# Revit family: Sanitary_Taps-And-Mixers_Sanindusa_Line-42_Wall-Concealed-Basin-Mixer
name_source: partatom
category: Plumbing Fixtures
revit_build: Autodesk Revit 2018 (Build: 20170223_1515(x64)
units: mm (PartAtom-declared; Revit-internal decimal feet)

## family parameters
Cut with Voids When Loaded = No
Host = Face
Part Type = Normal
Room Calculation Point = No
Round Connector Dimension = Use Diameter
Shared = No

## types (1)
- Sanitary_Taps-And-Mixers_Sanindusa_Line-42_Wall-Concealed-Basin-Mixer
    AssetType = Fixed
    BodyMaterial = Brass
    CartridgeType = D35 mm closed ceramic cartridge
    Color = Silver
    Constituents = Single lever concealed basin mixer.  2 x M/F 10/1x1/2 350mm stainless steel flexible supply hoses.
    Default Elevation = 1219 mm
    Description = A small diameter valve, with a free outlet, from which water is drawn.
    Element Type = FAUCET: A small diameter valve, with a free outlet, from which water is drawn.
    FaucetFunction = Mixed
    FaucetOperation = Other
    FaucetTopDescription = Single lever
    FaucetType = SprayMixing
    Features = Ceramic cartridge technology. Single lever mixer. To install on the wall Compatible pop up wastes (not included): 4V9111; 4V9711.
    Finish = Chrome plated
    FlowCoefficient = "water flow to 3 bar**: 13.5L/min.
(** total opening at 50% hot water + 50% cold water)"
    FlowRateMaximum = 3 Bar: 13.5 L/min
    InletConnectionType = 2 x M/F 10/1x1/2 350mm stainless steel flexible supply hoses
    Installation Instructions = https://www.tec.sanindusa.pt
    InstallationDate = 1900-12-31T23:59:59
    Manufacturer = Sanindusa
    ManufacturerName = Sanindusa
    ManufacturerURL = www.tec.sanindusa.pt
    Material = Brass
    Model = 5552301
    ModelNumber = 5552301
    ModelReference = Line 42
    Name = Line 42 concealed basin mixer
    NominalHeight = 105 mm  [stored 0.344488 ft]
    NominalLength = 209 mm  [stored 0.685696 ft]
    NominalWidth = 195 mm  [stored 0.639764 ft]
    OperatingMechanismMaterial = Brass
    Pre-defined type (IFC) = FAUCET
    ProductInformation = https://www.tec.sanindusa.pt
    ProductionYear = 2019
    Size = 209x195x105
    TestPressure = 10 bar
    Type (IFC) = IfcValveType
    URL = www.tec.sanindusa.pt
    Uniclass2015Version = Products v1.6
    ValveMechanism = UNSET
    ValveOperation = UNSET
    ValvePattern = UNSET
    Version = 1
    WarrantyDescription = https://www.tec.sanindusa.pt
    WarrantyDurationParts = 5
    WarrantyDurationUnit = year
    WarrantyStartDate = 1900-12-31T23:59:59
    Weight = 2.24 kg
    WorkingPressure = 3 bar

note: [stored X ft] marks values corroborated as IEEE doubles in the binary element streams (Revit-internal decimal feet)

## geometry (parser evidence)
native form markers: Sweep x7
no freeform markers — native parametric forms only
